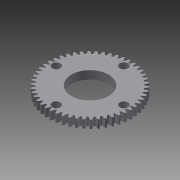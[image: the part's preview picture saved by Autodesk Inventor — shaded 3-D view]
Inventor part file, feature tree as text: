
AUTODESK INVENTOR PART (.ipt)
format: ipt  version: 2013 (Build 170138000, 138)  size: 431,104 bytes
history: native  units: in
note: dims shown in document units (in); Inventor stores cm internally (conversion verified against a paired STEP export)
features: extrude x1, sketch x1
ambient origin geometry x8: Origin, YZ Plane, XZ Plane, XY Plane, X Axis, Y Axis, Z Axis, Center Point
bodies: Solid1 (feature_tree)
feature tree (2):
  extrude  "Extrusion1"  Depth=0.26in
  sketch  "Sketch1"  dims[d1=2.09in d2=0.26in d3=0.26in d4=0.26in d5=0.26in d6=1.15in d7=0.25in d8=0.0in]
